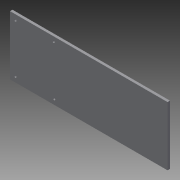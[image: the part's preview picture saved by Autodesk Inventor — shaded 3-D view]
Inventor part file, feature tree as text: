
AUTODESK INVENTOR PART (.ipt)
format: ipt  version: 2014 SP1 (Build 180222100, 222)  size: 87,040 bytes
history: native  units: in
note: dims shown in document units (in); Inventor stores cm internally (conversion verified against a paired STEP export)
features: extrude x1, sketch x1
ambient origin geometry x8: Origin, YZ Plane, XZ Plane, XY Plane, X Axis, Y Axis, Z Axis, Center Point
bodies: Body1 (feature_tree)
feature tree (2):
  extrude  "Extrusion2"  Depth=6.0in
  sketch  "Sketch1"  dims[d0=16.0in d1=6.0in d2=0.75in d3=45.0deg d4=0.75in d5=45.0deg d6=5.0in d7=0.75in d8=0.25in d10=0.25in d11=0.25in d15=5.0in d16=0.25in d17=0.25in d18=0.0in]
